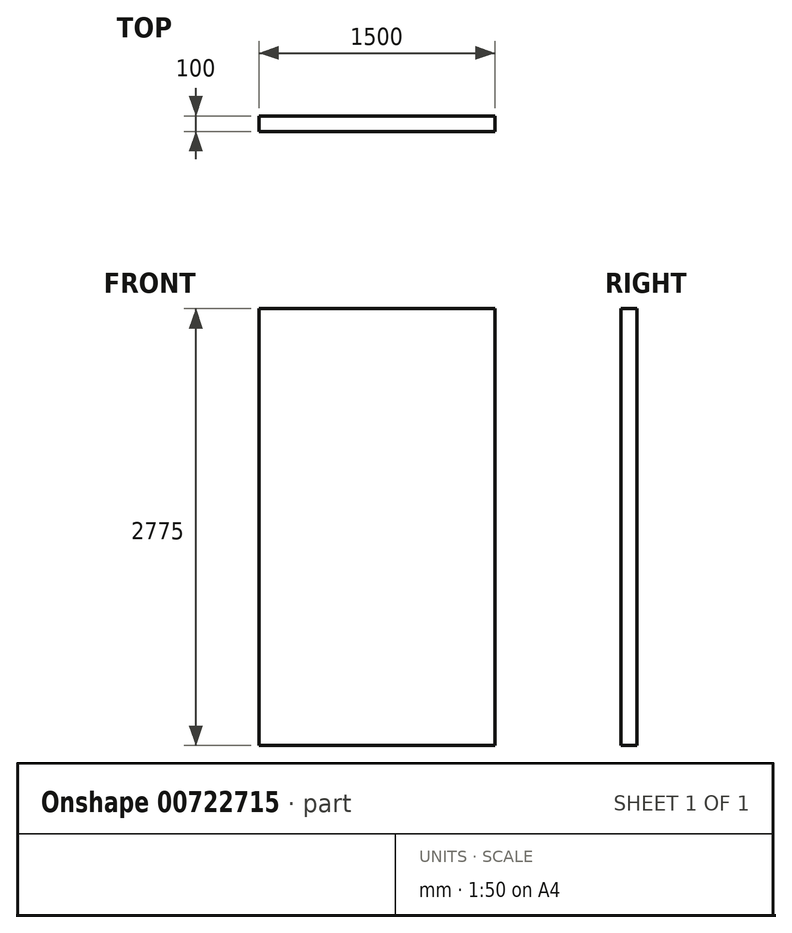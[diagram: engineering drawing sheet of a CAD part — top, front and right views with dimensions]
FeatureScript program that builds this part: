
annotation { "Feature Type Name" : "Feature", "Feature Type Description" : "" }
export const myFeature = defineFeature(function(context is Context, id is Id, definition is map)
    precondition{}
    {
        {
            var Q0;
            Q0=qCreatedBy(makeId("Front.planeOp"),FACE);
            var sketch = newSketch(context, id + "F0", { "sketchPlane" : qUnion([Q0])});
            skLineSegment(sketch, "E0.bottom", {"start": v(0, 0) * mm, "end": v(1500, 0) * mm});
            skLineSegment(sketch, "E0.top", {"start": v(0, 2775) * mm, "end": v(1500, 2775) * mm});
            skLineSegment(sketch, "E0.left", {"start": v(0, 0) * mm, "end": v(0, 2775) * mm});
            skLineSegment(sketch, "E0.right", {"start": v(1500, 0) * mm, "end": v(1500, 2775) * mm});
            skSolve(sketch);
        }
        {
            var Q0;
            Q0=makeQuery(id+"F0.imprint","IMPRINT",FACE,{"disambiguationData":[TD([[makeQuery(id+"F0.imprint","IMPRINT",EDGE,{"derivedFrom":sQuery(id+"F0.wireOp",EDGE,"E0.bottom")}),1.0]])]});
            extrude(context, id + "F1", {"entities" : qUnion([Q0]), "depth" : 100 * mm, "offsetDistance" : 25 * mm});
        }
    });
